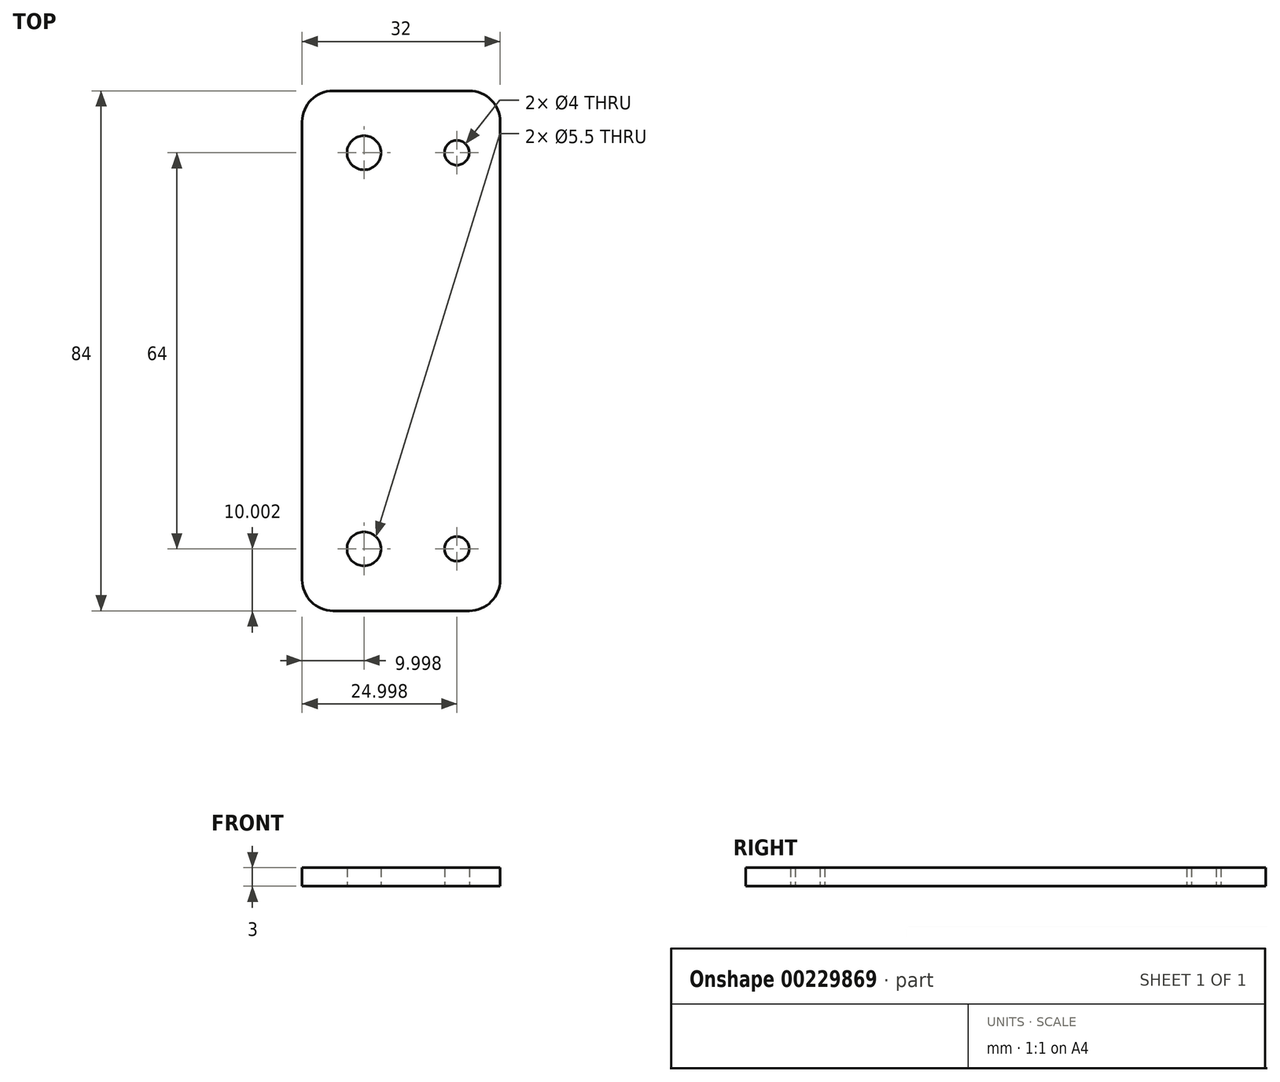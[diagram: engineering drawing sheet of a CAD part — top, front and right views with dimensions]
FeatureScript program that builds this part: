
annotation { "Feature Type Name" : "Feature", "Feature Type Description" : "" }
export const myFeature = defineFeature(function(context is Context, id is Id, definition is map)
    precondition{}
    {
        {
            var Q0;
            Q0=qCreatedBy(makeId("Top.planeOp"),FACE);
            var sketch = newSketch(context, id + "F0", { "sketchPlane" : qUnion([Q0])});
            skLineSegment(sketch, "E0.right", {"start": v(-79.61, -22.39) * mm, "end": v(-79.61, 21.61) * mm});
            skLineSegment(sketch, "E1.right", {"start": v(74.39, -8.39) * mm, "end": v(74.39, -28.39) * mm});
            skLineSegment(sketch, "E2.top", {"start": v(-74.61, 41.61) * mm, "end": v(-64.61, 41.61) * mm});
            skLineSegment(sketch, "E2.left", {"start": v(-79.61, 21.61) * mm, "end": v(-79.61, 36.61) * mm});
            skLineSegment(sketch, "E3.top", {"start": v(-74.61, -42.39) * mm, "end": v(-64.61, -42.39) * mm});
            skLineSegment(sketch, "E3.left", {"start": v(-79.61, -22.39) * mm, "end": v(-79.61, -37.39) * mm});
            skLineSegment(sketch, "E4.top", {"start": v(59.39, 41.61) * mm, "end": v(69.39, 41.61) * mm});
            skLineSegment(sketch, "E4.right", {"start": v(74.39, 21.61) * mm, "end": v(74.39, 36.61) * mm});
            skLineSegment(sketch, "E5.top", {"start": v(59.39, -42.39) * mm, "end": v(69.39, -42.39) * mm});
            skLineSegment(sketch, "E5.right", {"start": v(74.39, -22.39) * mm, "end": v(74.39, -37.39) * mm});
            skPoint(sketch, "E6.positionSnap1", {"position": v(-67.11, 41.61) * mm});
            skPoint(sketch, "E7", {"position": v(64.39, 31.61) * mm});
            skPoint(sketch, "E7.positionSnap0", {"position": v(64.39, 41.61) * mm});
            skPoint(sketch, "E7.positionSnap1", {"position": v(74.39, 31.61) * mm});
            skPoint(sketch, "E8", {"position": v(64.39, -32.39) * mm});
            skPoint(sketch, "E8.positionSnap0", {"position": v(74.39, -32.39) * mm});
            skPoint(sketch, "E8.positionSnap1", {"position": v(64.39, -42.39) * mm});
            skPoint(sketch, "E9", {"position": v(-69.61, -32.39) * mm});
            skPoint(sketch, "E9.positionSnap0", {"position": v(-79.61, -32.39) * mm});
            skPoint(sketch, "E9.positionSnap1", {"position": v(-69.61, -42.39) * mm});
            skCircle(sketch, "E10", {"center": v(64.39, 31.61) * mm, "radius": 2.75 * mm});
            skCircle(sketch, "E11", {"center": v(64.39, -32.39) * mm, "radius": 2.75 * mm});
            skCircle(sketch, "E12", {"center": v(-69.61, -32.39) * mm, "radius": 2.75 * mm});
            skPoint(sketch, "E13.visualSharp", {"position": v(54.39, 41.61) * mm});
            skPoint(sketch, "E14.visualSharp", {"position": v(74.39, 41.61) * mm});
            skArc(sketch, "E14.filletArc", {"start": v(74.39, 36.61) * mm, "mid": v(72.92, 40.15) * mm, "end": v(69.39, 41.61) * mm});
            skPoint(sketch, "E15.visualSharp", {"position": v(74.39, -42.39) * mm});
            skArc(sketch, "E15.filletArc", {"start": v(69.39, -42.39) * mm, "mid": v(72.92, -40.92) * mm, "end": v(74.39, -37.39) * mm});
            skPoint(sketch, "E16.visualSharp", {"position": v(-79.61, -42.39) * mm});
            skArc(sketch, "E16.filletArc", {"start": v(-79.61, -37.39) * mm, "mid": v(-78.15, -40.92) * mm, "end": v(-74.61, -42.39) * mm});
            skPoint(sketch, "E17.visualSharp", {"position": v(-79.61, 41.61) * mm});
            skArc(sketch, "E17.filletArc", {"start": v(-74.61, 41.61) * mm, "mid": v(-78.15, 40.15) * mm, "end": v(-79.61, 36.61) * mm});
            skPoint(sketch, "E18.visualSharp", {"position": v(-54.61, 41.61) * mm});
            skLineSegment(sketch, "E19.left", {"start": v(-79.61, 36.61) * mm, "end": v(-79.61, -8.39) * mm});
            skLineSegment(sketch, "E20.left", {"start": v(74.39, 36.61) * mm, "end": v(74.39, -13.39) * mm});
            skCircle(sketch, "E21", {"center": v(-69.61, 31.61) * mm, "radius": 2.75 * mm});
            skPoint(sketch, "E22", {"position": v(-54.61, -32.39) * mm});
            skPoint(sketch, "E23", {"position": v(-54.61, 31.61) * mm});
            skPoint(sketch, "E24", {"position": v(54.39, 31.61) * mm});
            skPoint(sketch, "E25", {"position": v(54.39, -32.39) * mm});
            skCircle(sketch, "E26", {"center": v(54.39, 31.61) * mm, "radius": 2 * mm});
            skCircle(sketch, "E27", {"center": v(54.39, -32.39) * mm, "radius": 2 * mm});
            skCircle(sketch, "E28", {"center": v(-54.61, -32.39) * mm, "radius": 2 * mm});
            skCircle(sketch, "E29", {"center": v(-54.61, 31.61) * mm, "radius": 2 * mm});
            skLineSegment(sketch, "E30", {"start": v(47.39, -37.39) * mm, "end": v(47.39, 36.61) * mm});
            skLineSegment(sketch, "E31", {"start": v(-47.61, -37.39) * mm, "end": v(-47.61, 36.61) * mm});
            skLineSegment(sketch, "E32", {"start": v(-64.61, -42.39) * mm, "end": v(-52.61, -42.39) * mm});
            skLineSegment(sketch, "E33", {"start": v(-67.11, 41.61) * mm, "end": v(-52.61, 41.61) * mm});
            skLineSegment(sketch, "E34", {"start": v(52.39, 41.61) * mm, "end": v(59.39, 41.61) * mm});
            skLineSegment(sketch, "E35", {"start": v(52.39, -42.39) * mm, "end": v(59.39, -42.39) * mm});
            skPoint(sketch, "E36.visualSharp", {"position": v(-47.61, 41.61) * mm});
            skArc(sketch, "E36.filletArc", {"start": v(-47.61, 36.61) * mm, "mid": v(-49.08, 40.15) * mm, "end": v(-52.61, 41.61) * mm});
            skPoint(sketch, "E37.visualSharp", {"position": v(-47.61, -42.39) * mm});
            skArc(sketch, "E37.filletArc", {"start": v(-52.61, -42.39) * mm, "mid": v(-49.08, -40.92) * mm, "end": v(-47.61, -37.39) * mm});
            skPoint(sketch, "E38.visualSharp", {"position": v(47.39, 41.61) * mm});
            skArc(sketch, "E38.filletArc", {"start": v(52.39, 41.61) * mm, "mid": v(48.85, 40.15) * mm, "end": v(47.39, 36.61) * mm});
            skPoint(sketch, "E39.visualSharp", {"position": v(47.39, -42.39) * mm});
            skArc(sketch, "E39.filletArc", {"start": v(47.39, -37.39) * mm, "mid": v(48.85, -40.92) * mm, "end": v(52.39, -42.39) * mm});
            skSolve(sketch);
        }
        {
            var Q0;
            Q0=makeQuery(id+"F0.imprint","IMPRINT",FACE,{"disambiguationData":[TD([[makeQuery(id+"F0.imprint","IMPRINT",EDGE,{"derivedFrom":sQuery(id+"F0.wireOp",EDGE,"E0.right")}),-1.0]])]});
            extrude(context, id + "F1", {"entities" : qUnion([Q0]), "depth" : 3 * mm});
        }
        {
            var Q0;
            {var subQ4=sQuery(id+"F0.wireOp",EDGE,"E1.right");Q0=makeQuery(id+"F0.imprint","IMPRINT",FACE,{"disambiguationData":[TD([[makeQuery(id+"F0.imprint","IMPRINT",EDGE,{"derivedFrom":subQ4}),-1.0]])]});}
            extrude(context, id + "F2", {"entities" : qUnion([Q0]), "depth" : 3 * mm});
        }
        {
            var Q0;
            Q0=makeQuery(id+"F2.opExtrude","SWEPT_BODY",BODY,{"disambiguationData":[OSD([sQuery(id+"F0.wireOp",EDGE,"E1.right"),sQuery(id+"F0.wireOp",EDGE,"E4.top"),sQuery(id+"F0.wireOp",EDGE,"E5.top"),sQuery(id+"F0.wireOp",EDGE,"E5.right"),sQuery(id+"F0.wireOp",EDGE,"E10"),sQuery(id+"F0.wireOp",EDGE,"E11"),sQuery(id+"F0.wireOp",EDGE,"E14.filletArc"),sQuery(id+"F0.wireOp",EDGE,"E15.filletArc"),sQuery(id+"F0.wireOp",EDGE,"E20.left"),sQuery(id+"F0.wireOp",EDGE,"E26"),sQuery(id+"F0.wireOp",EDGE,"E27"),sQuery(id+"F0.wireOp",EDGE,"E30"),sQuery(id+"F0.wireOp",EDGE,"E34"),sQuery(id+"F0.wireOp",EDGE,"E35"),sQuery(id+"F0.wireOp",EDGE,"E38.filletArc"),sQuery(id+"F0.wireOp",EDGE,"E39.filletArc")])]});
            deleteBodies(context, id + "F3", {"entities" : qUnion([Q0])});
        }
    });
